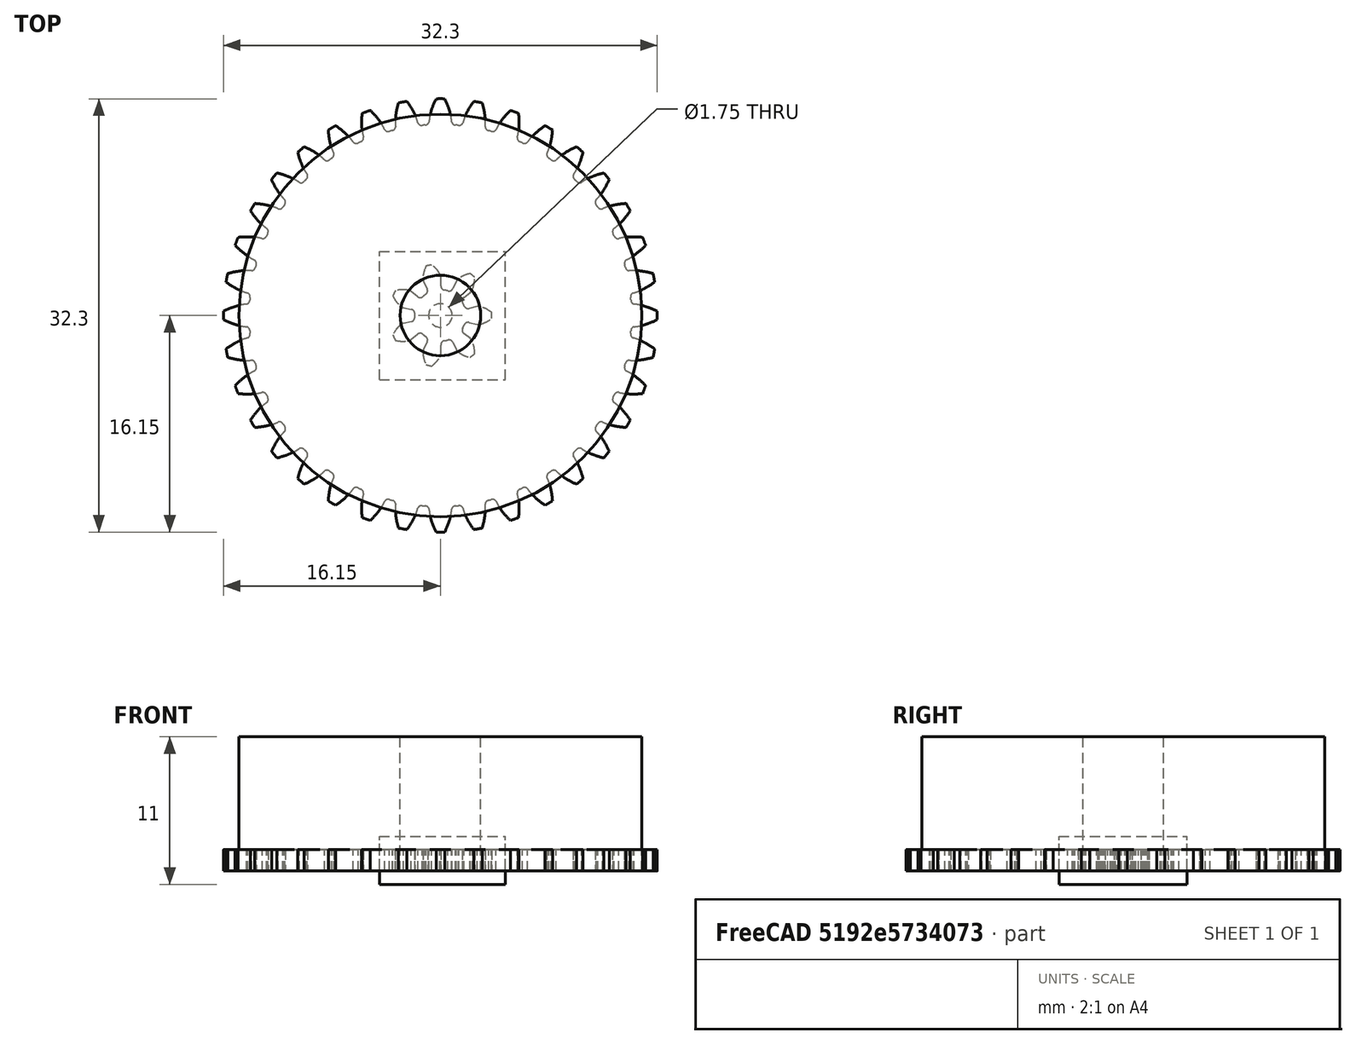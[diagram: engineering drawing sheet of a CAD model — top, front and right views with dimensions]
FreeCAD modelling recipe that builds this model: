
FCSTD DOCUMENT  (FreeCAD 0.18R16033 (Git))
Label: gear
License: All rights reserved
LicenseURL: http://en.wikipedia.org/wiki/All_rights_reserved
objects: Part::Cylinder×3, Path::FeaturePython×3, Part::Part2DObjectPython×2, Part::Extrusion×2, Part::FeaturePython×2, App::FeaturePython×1, App::DocumentObjectGroup×1, Part::Cut×1, Path::FeatureCompoundPython×1
note: 11 computed .brp shape members not serialized (recipe doc carries the construction recipe); baked Part::Feature solids carry a one-line shape summary decoded from their .brp

FEATURE [Part::Part2DObjectPython] InvoluteGear  # Draft 2D object (typed FeaturePython)
  ExternalGear = true
  HighPrecision = true
  Modules = 0.85
  NumberOfTeeth = 7
  PressureAngle = 20
FEATURE [Part::Extrusion] Extrude
  Base = -> InvoluteGear
  Dir = (0,0,1)
  DirMode = 2
  FaceMakerClass = Part::FaceMakerBullseye
  LengthFwd = 1.59
  LengthRev = 0
  Solid = true
  Symmetric = false
FEATURE [App::FeaturePython] SetupSheet  # Path/CAM operation (typed FeaturePython)
  ClearanceHeightExpression = OpStockZMax+SetupSheet.ClearanceHeightOffset
  ClearanceHeightOffset = 5
  FinalDepthExpression = OpFinalDepth
  HorizRapid = 0
  SafeHeightExpression = OpStockZMax+SetupSheet.SafeHeightOffset
  SafeHeightOffset = 3
  StartDepthExpression = OpStartDepth
  StepDownExpression = OpToolDiameter
  VertRapid = 0
FEATURE [Part::FeaturePython] Clone  label="Model-Extrude"  # Draft clone (typed FeaturePython)
  AttacherType = Attacher::AttachEngine3D
  Fuse = false
  Objects = -> [Extrude]
  PathResource = Model
  Scale = (1,1,1)
FEATURE [App::DocumentObjectGroup] Model
  Group = -> [Clone]
FEATURE [Part::Cylinder] Cylinder
  Angle = 360
  AttacherType = Attacher::AttachEngine3D
  Height = 10
  Radius = 3
FEATURE [Part::Part2DObjectPython] InvoluteGear001  # Draft 2D object (typed FeaturePython)
  ExternalGear = true
  HighPrecision = true
  Modules = 0.85
  NumberOfTeeth = 36
  PressureAngle = 20
FEATURE [Part::Extrusion] Extrude001
  Base = -> InvoluteGear001
  Dir = (0,0,1)
  DirMode = 2
  FaceMakerClass = Part::FaceMakerBullseye
  LengthFwd = 1.59
  LengthRev = 0
  Solid = true
  Symmetric = false
FEATURE [Part::Cylinder] Cylinder001
  Angle = 360
  AttacherType = Attacher::AttachEngine3D
  Height = 10
  Radius = 15
FEATURE [Part::Cylinder] Cylinder002
  Angle = 360
  AttacherType = Attacher::AttachEngine3D
  Height = 10
  Radius = 0.875
  expr: Radius = 1.75 / 2
FEATURE [Part::Cut] Cut
  Base = -> Extrude
  Tool = -> Cylinder002
FEATURE [Path::FeaturePython] T5__31_End_mill  label="T5: 31 End mill"  # Path/CAM operation (typed FeaturePython)
  HorizFeed = 3
  HorizRapid = 0
  SpindleDir = 0
  SpindleSpeed = 24000
  ToolNumber = 1
  VertFeed = 0.5
  VertRapid = 0
  expr: HorizRapid = SetupSheet.HorizRapid
  expr: VertRapid = SetupSheet.VertRapid
FEATURE [Path::FeaturePython] Contour  # Path/CAM operation (typed FeaturePython)
  Active = true
  AreaParams:
    OpenMode = 0
    Angle = 45.0
    MinArcPoints = 4
    Coplanar = 2
    Tolerance = 1e-07
    CleanDistance = 0.0
    PocketExtraOffset = 0.0
    RoundPrecision = 0.0
    AngleShift = 0.0
    SubjectFill = 0
    PocketMode = 0
    PocketLastStepover = 0.0
    Simplify = False
    SectionTolerance = 1e-06
    MaxArcPoints = 100
    Offset = 0.395
    Accuracy = 0.01
    LastStepover = 0.0
    PocketStepover = 0.0
    ClipFill = 0
    ToolRadius = 1.0
    Outline = False
    ClipperScale = 10000000.0
    FromCenter = False
    Explode = False
    EndType = 0
    Shift = 0.0
    ExtraPass = 0
    Project = False
    JoinType = 0
    Thicken = False
    Stepdown = 1.0
    SectionMode = 2
    MiterLimit = 2.0
    Deflection = 0.01
    Reorient = True
    FitArcs = True
    SectionCount = -1
    SectionOffset = 0.0
    Stepover = 0.0
    Unit = 1.0
    Fill = 0
  ClearanceHeight = 7.59
  Direction = 0
  FinalDepth = -0.1
  JoinType = 0
  MiterLimit = 0.1
  OffsetExtra = 0
  OpFinalDepth = -1
  OpStartDepth = 2.59
  OpStockZMax = 2.59
  OpStockZMin = -1
  OpToolDiameter = 0.79
  PathParams = {'resume_height': 5.59, 'feedrate': 3.0, 'verbose': True, 'orientation': 1, 'return_end': True, 'preamble': False, 'retraction': 7.59, 'feedrate_v': 0.5}
  SafeHeight = 5.59
  Side = 0
  StartDepth = 2.59
  StartPoint = (0,0,0)
  StepDown = 0.3
  ToolController = -> T5__31_End_mill
  UseComp = true
  UseStartPoint = false
  expr: ClearanceHeight = OpStockZMax + SetupSheet.ClearanceHeightOffset
  expr: SafeHeight = OpStockZMax + SetupSheet.SafeHeightOffset
  expr: StepDown = 0.3
  expr: FinalDepth = -0.1
  expr: StartDepth = OpStartDepth
FEATURE [Path::FeatureCompoundPython] Operations  # Path/CAM operation (typed FeaturePython)
  Group = -> [Contour]
  UsePlacements = false
FEATURE [Part::FeaturePython] Stock  # WARN: FeaturePython — macro-defined, semantics opaque (R4)
  Base = -> Model
  ExtXneg = 1
  ExtXpos = 1
  ExtYneg = 1
  ExtYpos = 1
  ExtZneg = 1
  ExtZpos = 1
  Placement = pos=(-3.53587,-3.77284,0) rot=(0,0,1;0rad)
  StockType = FromBase
FEATURE [Path::FeaturePython] Job  # Path/CAM operation (typed FeaturePython)
  GeometryTolerance = 0.01
  Model = -> Model
  Operations = -> Operations
  PostProcessor = 1
  SetupSheet = -> SetupSheet
  Stock = -> Stock
  ToolController = -> [T5__31_End_mill]
